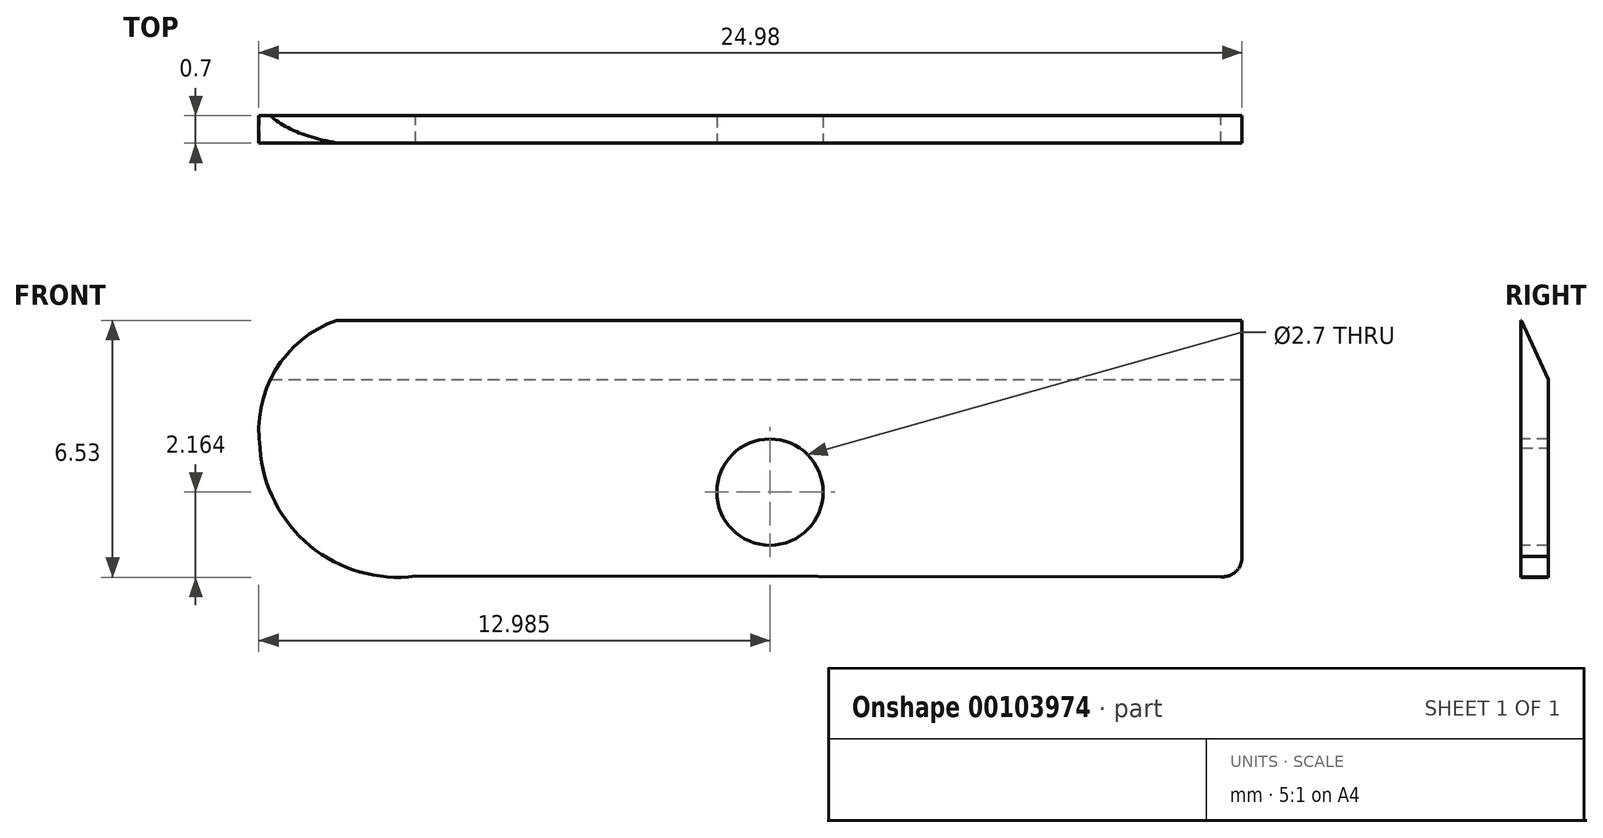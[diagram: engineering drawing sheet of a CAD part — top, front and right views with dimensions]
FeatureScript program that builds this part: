
annotation { "Feature Type Name" : "Feature", "Feature Type Description" : "" }
export const myFeature = defineFeature(function(context is Context, id is Id, definition is map)
    precondition{}
    {
        {
            var Q0;
            Q0=qCreatedBy(makeId("Front.planeOp"),FACE);
            var sketch = newSketch(context, id + "F0", { "sketchPlane" : qUnion([Q0])});
            skCircle(sketch, "E0", {"center": v(-12.47, 2.15) * mm, "radius": 1.35 * mm});
            skArc(sketch, "E1", {"start": v(-0.54, -0.02) * mm, "mid": v(-0.16, 0.12) * mm, "end": v(0, 0.5) * mm});
            skLineSegment(sketch, "E2", {"start": v(0, 6.5) * mm, "end": v(0, 0.5) * mm});
            skArc(sketch, "E3", {"start": v(-23, 6.5) * mm, "mid": v(-24.56, 5.23) * mm, "end": v(-24.95, 3.25) * mm});
            skArc(sketch, "E4", {"start": v(-24.95, 3.25) * mm, "mid": v(-23.68, 0.77) * mm, "end": v(-21, 0) * mm});
            skLineSegment(sketch, "E5", {"start": v(0, 6.5) * mm, "end": v(-23, 6.5) * mm});
            skLineSegment(sketch, "E6", {"start": v(-0.54, -0.02) * mm, "end": v(-21, 0) * mm});
            skLineSegment(sketch, "E7", {"start": v(0, 4.98) * mm, "end": v(-24.7, 4.98) * mm});
            skSolve(sketch);
        }
        {
            var Q0;
            Q0=makeQuery(id+"F0.imprint","IMPRINT",FACE,{"disambiguationData":[TD([[makeQuery(id+"F0.imprint","IMPRINT",EDGE,{"derivedFrom":sQuery(id+"F0.wireOp",EDGE,"E0")}),1.0]])]});
            var Q1;
            Q1=makeQuery(id+"F0.imprint","IMPRINT",FACE,{"disambiguationData":[TD([[makeQuery(id+"F0.imprint","IMPRINT",EDGE,{"derivedFrom":sQuery(id+"F0.wireOp",EDGE,"E0")}),-1.0]])]});
            var Q2;
            {var subQ0=sQuery(id+"F0.wireOp",EDGE,"E5");Q2=makeQuery(id+"F0.imprint","IMPRINT",FACE,{"disambiguationData":[TD([[makeQuery(id+"F0.imprint","IMPRINT",EDGE,{"derivedFrom":subQ0}),1.0]])]});}
            extrude(context, id + "F1", {"entities" : qUnion([Q0, Q1, Q2]), "depth" : 0.7 * mm});
        }
        {
            var Q0;
            Q0=makeQuery(id+"F1.opExtrude","CAP_FACE",FACE,{"disambiguationData":[OSD([sQuery(id+"F0.wireOp",EDGE,"E1"),sQuery(id+"F0.wireOp",EDGE,"E2"),sQuery(id+"F0.wireOp",EDGE,"E3"),sQuery(id+"F0.wireOp",EDGE,"E4"),sQuery(id+"F0.wireOp",EDGE,"E5"),sQuery(id+"F0.wireOp",EDGE,"E6")])],"isStart":false});
            var sketch = newSketch(context, id + "F2", { "sketchPlane" : qUnion([Q0])});
            skCircle(sketch, "E8", {"center": v(-12, 2.13) * mm, "radius": 1.35 * mm});
            skSolve(sketch);
        }
        {
            var Q0;
            Q0=makeQuery(id+"F2.imprint","IMPRINT",FACE,{"disambiguationData":[TD([[makeQuery(id+"F2.imprint","IMPRINT",EDGE,{"derivedFrom":sQuery(id+"F2.wireOp",EDGE,"E8")}),1.0]])]});
            var Q1;
            Q1=sQuery(id+"F2.wireOp",EDGE,"E8");
            extrude(context, id + "F3", {"entities" : qUnion([Q0]), "operationType" : NewBodyOperationType.REMOVE, "surfaceEntities" : qUnion([Q1]), "oppositeDirection" : true, "depth" : 25 * mm});
        }
        {
            var Q0;
            Q0=qCreatedBy(makeId("Right.planeOp"),FACE);
            var sketch = newSketch(context, id + "F4", { "sketchPlane" : qUnion([Q0])});
            skLineSegment(sketch, "E9", {"start": v(0, 5) * mm, "end": v(-0.7, 6.52) * mm});
            skLineSegment(sketch, "E10", {"start": v(0, 0) * mm, "end": v(0, 5) * mm});
            skLineSegment(sketch, "E11", {"start": v(0, 5) * mm, "end": v(0, 6.52) * mm});
            skLineSegment(sketch, "E12", {"start": v(0, 6.52) * mm, "end": v(-0.7, 6.52) * mm});
            skSolve(sketch);
        }
        {
            var Q0;
            Q0=makeQuery(id+"F4.imprint","IMPRINT",FACE,{"disambiguationData":[TD([[makeQuery(id+"F4.imprint","IMPRINT",EDGE,{"derivedFrom":sQuery(id+"F4.wireOp",EDGE,"E9")}),-1.0]])]});
            var Q1;
            Q1=sQuery(id+"F4.wireOp",EDGE,"E9");
            var Q2;
            Q2=sQuery(id+"F4.wireOp",EDGE,"E12");
            var Q3;
            Q3=sQuery(id+"F4.wireOp",EDGE,"E11");
            extrude(context, id + "F5", {"entities" : qUnion([Q0]), "operationType" : NewBodyOperationType.REMOVE, "surfaceEntities" : qUnion([Q1, Q2, Q3]), "oppositeDirection" : true, "depth" : 25 * mm});
        }
    });
